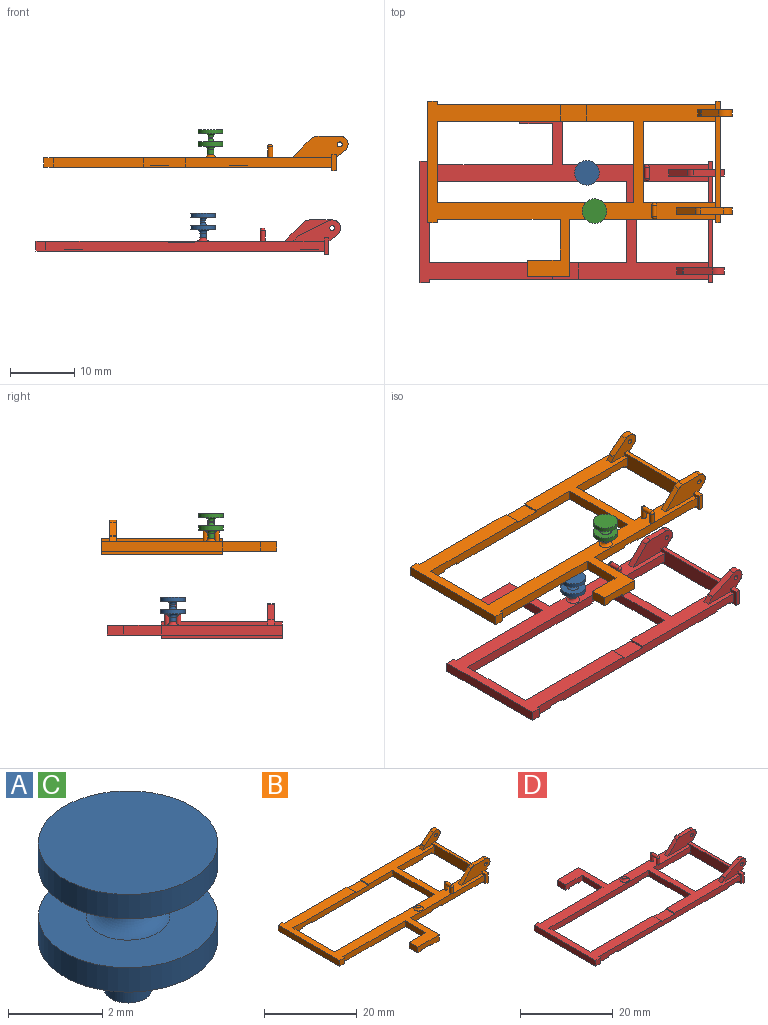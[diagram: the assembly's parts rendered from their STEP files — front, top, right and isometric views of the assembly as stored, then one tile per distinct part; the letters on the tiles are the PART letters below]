
ASSEMBLY  parts=4 mates=4
PART A: 12 faces, bbox 3.8x3.8x3.8 mm
  f0: cylinder r=0.51mm len=1.02mm, axis (0,0,-1), area 2.4mm2, adj f1,f11
  f1: plane 1.02x1.02mm, normal (0,0,-1), area 0.8mm2, adj f0
  f2: cylinder r=1.91mm len=3.81mm, axis (0,0,-1), area 7.6mm2, adj f3,f4
  f3: plane 3.81x3.81mm, normal (0,0,1), area 8.9mm2, adj f2,f9
  f4: plane 3.81x3.81mm, normal (0,0,-1), area 8.2mm2, adj f2,f11
  f5: cylinder r=0.38mm len=0.76mm, axis (0,0,-1), area 0.6mm2, adj f9,f10
  f6: cylinder r=1.91mm len=3.81mm, axis (0,0,-1), area 7.6mm2, adj f7,f8
  f7: plane 3.81x3.81mm, normal (0,0,1), area 11.4mm2, adj f6
  f8: plane 3.81x3.81mm, normal (0,0,-1), area 8.9mm2, adj f6,f10
  f9: torus R=0.89mm, axis (0,0,1), area 2.8mm2, adj f3,f5
  f10: torus R=0.89mm, axis (0,0,1), area 2.8mm2, adj f5,f8
  f11: torus R=1.02mm, axis (0,0,1), area 3.5mm2, adj f0,f4
PART B: 71 faces, bbox 47.2x27.2x5.3 mm
  f0: plane 44.7x27.18mm, normal (0,0,1), area 270.3mm2, adj f1,f2,f8,f9,f10,f16,f21,f22
  f1: plane 43.18x1.52mm, normal (0,1,0), area 63.4mm2, adj f0,f4,f5,f6,f16,f21,f47,f48
  f2: plane 5.3x3.3mm, normal (0,1,0), area 9.7mm2, adj f0,f11,f12,f13,f14,f15,f16,f17
  f3: cylinder r=1.27mm len=2.26mm, axis (0,-1,0), area 3.2mm2, adj f18,f41,f42,f56
  f4: plane 2.54x0.89mm, normal (0,0,-1), area 2.3mm2, adj f1,f16,f34,f50
  f5: plane 37.47x17.78mm, normal (0,0,-1), area 138.4mm2, adj f1,f10,f16,f30,f33,f34,f36,f37
  f6: plane 28.83x27.18mm, normal (0,0,-1), area 121.9mm2, adj f1,f8,f9,f10,f21,f22,f23,f24
  f7: plane 2.54x1.14mm, normal (0,0,-1), area 2.9mm2, adj f8,f9,f28,f53
  f8: plane 5.08x1.52mm, normal (0,1,0), area 7mm2, adj f0,f6,f7,f27,f28,f53,f54,f55
  f9: plane 6.6x1.52mm, normal (0,-1,0), area 9.4mm2, adj f0,f6,f7,f28,f29,f53,f54,f55
  f10: plane 30.48x1.52mm, normal (0,1,0), area 45.7mm2, adj f0,f5,f6,f35,f37,f44,f45,f46
  f11: plane 1.3x1.04mm, normal (0.62,0,-0.78), area 1.7mm2, adj f2,f12,f15,f43
  f12: cylinder r=1.27mm len=2.26mm, axis (0,-1,0), area 4.1mm2, adj f2,f11,f14,f43
  f13: cylinder r=0.38mm len=1.02mm, axis (0,-1,0), area 2.4mm2, adj f2,f43
  f14: plane 2.65x2.12mm, normal (-0.62,0,0.78), area 3.4mm2, adj f2,f12,f43,f59
  f15: plane 18.8x2.54mm, normal (1,0,0), area 46.7mm2, adj f2,f11,f17,f18,f20,f31,f32,f39
  f16: plane 18.8x2.54mm, normal (-1,0,0), area 39mm2, adj f0,f1,f2,f4,f5,f17,f20,f30
  f17: plane 1.27x0.76mm, normal (0,0,1), area 1mm2, adj f2,f15,f16,f32
  f18: plane 1.3x1.04mm, normal (0.62,0,-0.78), area 1.7mm2, adj f3,f15,f41,f42
  f19: cylinder r=0.38mm len=1.02mm, axis (0,-1,0), area 2.4mm2, adj f41,f42
  f20: plane 14.22x0.76mm, normal (0,0,1), area 10.8mm2, adj f15,f16,f42,f43
  f21: plane 1.52x0.51mm, normal (1,0,0), area 0.8mm2, adj f0,f1,f6,f22
  f22: plane 1.52x1.52mm, normal (0,1,0), area 2.3mm2, adj f0,f6,f21,f23
  f23: plane 18.8x1.52mm, normal (-1,0,0), area 28.6mm2, adj f0,f6,f22,f24
  f24: plane 1.52x1.52mm, normal (0,-1,0), area 2.3mm2, adj f0,f6,f23,f25
  f25: plane 1.52x0.51mm, normal (1,0,0), area 0.8mm2, adj f0,f6,f24,f26
  f26: plane 19.05x1.52mm, normal (0,-1,0), area 29mm2, adj f0,f6,f25,f27
  f27: plane 6.35x1.52mm, normal (-1,0,0), area 9.7mm2, adj f0,f6,f8,f26
  f28: plane 2.54x1.52mm, normal (-1,0,0), area 3.9mm2, adj f0,f7,f8,f9
  f29: plane 8.89x1.52mm, normal (1,0,0), area 13.5mm2, adj f0,f6,f9,f30
  f30: plane 22.61x1.52mm, normal (0,-1,0), area 33.7mm2, adj f0,f5,f6,f16,f29,f44,f45,f46
  f31: plane 2.54x0.76mm, normal (0,-1,0), area 1.9mm2, adj f15,f16,f39,f40
  f32: plane 2.54x0.76mm, normal (0,1,0), area 1.9mm2, adj f15,f16,f17,f39
  f33: plane 12.7x1.52mm, normal (1,0,0), area 19.4mm2, adj f0,f5,f34,f38
  f34: plane 11.18x1.52mm, normal (0,-1,0), area 16.3mm2, adj f0,f4,f5,f16,f33,f50,f51,f52
  f35: plane 12.7x1.52mm, normal (1,0,0), area 19.4mm2, adj f0,f6,f10,f36
  f36: plane 30.48x1.52mm, normal (0,-1,0), area 44.7mm2, adj f0,f5,f6,f35,f37,f47,f48,f49
  f37: plane 12.7x1.52mm, normal (-1,0,0), area 19.4mm2, adj f0,f5,f10,f36
  f38: plane 11.18x1.52mm, normal (0,1,0), area 17mm2, adj f0,f5,f16,f33
  f39: plane 18.8x0.76mm, normal (0,0,-1), area 14.3mm2, adj f15,f16,f31,f32
  f40: plane 1.27x0.76mm, normal (0,0,1), area 1mm2, adj f15,f16,f31,f41
  f41: plane 8.65x3.3mm, normal (0,-1,0), area 20.6mm2, adj f0,f3,f15,f16,f18,f19,f40,f56
  f42: plane 8.65x3.3mm, normal (0,1,0), area 20.6mm2, adj f0,f3,f15,f16,f18,f19,f20,f56
  f43: plane 5.3x3.3mm, normal (0,-1,0), area 9.7mm2, adj f0,f11,f12,f13,f14,f15,f16,f20
  f44: plane 2.54x0.25mm, normal (1,0,0), area 0.6mm2, adj f6,f10,f30,f46
  f45: plane 2.54x0.25mm, normal (-1,0,0), area 0.6mm2, adj f5,f10,f30,f46
  f46: plane 2.79x2.54mm, normal (0,0,-1), area 7.1mm2, adj f10,f30,f44,f45
  f47: plane 2.54x0.25mm, normal (-1,0,0), area 0.6mm2, adj f1,f5,f36,f49
  f48: plane 2.54x0.25mm, normal (1,0,0), area 0.6mm2, adj f1,f6,f36,f49
  f49: plane 2.79x2.54mm, normal (0,0,-1), area 7.1mm2, adj f1,f36,f47,f48
  f50: plane 2.54x0.25mm, normal (-1,0,0), area 0.6mm2, adj f1,f4,f34,f52
  f51: plane 2.54x0.25mm, normal (1,0,0), area 0.6mm2, adj f1,f5,f34,f52
  f52: plane 2.79x2.54mm, normal (0,0,-1), area 7.1mm2, adj f1,f34,f50,f51
  f53: plane 2.54x0.25mm, normal (1,0,0), area 0.6mm2, adj f7,f8,f9,f55
  f54: plane 2.54x0.25mm, normal (-1,0,0), area 0.6mm2, adj f6,f8,f9,f55
  f55: plane 2.79x2.54mm, normal (0,0,-1), area 7.1mm2, adj f8,f9,f53,f54
  f56: plane 3.56x1.02mm, normal (0,0,1), area 3.6mm2, adj f3,f41,f42,f57
  f57: cylinder r=1.27mm len=1.02mm, axis (0,-1,0), area 1mm2, adj f41,f42,f56,f58
  f58: plane 2.93x2.93mm, normal (-0.71,0,0.71), area 4.2mm2, adj f0,f41,f42,f57
  f59: cylinder r=0.51mm len=1.02mm, axis (0,1,0), area 0.2mm2, adj f2,f14,f43,f60
  f60: plane 1.02x0.77mm, normal (-0.85,0,0.52), area 0.9mm2, adj f0,f2,f43,f59
  f61: plane 2.54x0.25mm, normal (-1,0,0), area 0.6mm2, adj f0,f1,f36,f63
  f62: plane 2.54x0.25mm, normal (1,0,0), area 0.6mm2, adj f0,f1,f36,f63
  f63: plane 4.06x2.54mm, normal (0,0,1), area 10.3mm2, adj f1,f36,f61,f62
  f64: plane 1.02x1.02mm, normal (0,0,1), area 0.8mm2, adj f65
  f65: torus R=1.02mm, axis (0,0,1), area 3.5mm2, adj f0,f64
  f66: cylinder r=0.38mm len=1.65mm, axis (0,0,-1), area 3.7mm2, adj f0,f69,f70
  f67: sphere r=0.38mm, area 0.5mm2, adj f68,f70
  f68: cylinder r=0.38mm len=1.65mm, axis (0,0,1), area 3.7mm2, adj f0,f67,f70
  f69: sphere r=0.38mm, area 0.5mm2, adj f66,f70
  f70: cylinder r=0.38mm len=1.78mm, axis (0,-1,0), area 3.7mm2, adj f66,f67,f68,f69
PART C: same geometry as A
PART D: 71 faces, bbox 47.2x27.2x5.3 mm
  f0: plane 44.7x27.18mm, normal (0,0,1), area 268.2mm2, adj f2,f3,f8,f9,f10,f11,f16,f22
  f1: plane 4.57x2.21mm, normal (-0.44,0,0.9), area 5.2mm2, adj f2,f19,f41,f62
  f2: plane 7.37x3.3mm, normal (0,-1,0), area 13.4mm2, adj f0,f1,f15,f16,f18,f19,f20,f40
  f3: plane 30.48x1.52mm, normal (0,1,0), area 44.7mm2, adj f0,f4,f6,f35,f37,f44,f45,f46
  f4: plane 28.83x27.18mm, normal (0,0,-1), area 121.9mm2, adj f3,f8,f9,f10,f22,f23,f24,f25
  f5: plane 2.54x1.14mm, normal (0,0,-1), area 2.9mm2, adj f9,f10,f32,f54
  f6: plane 37.47x17.78mm, normal (0,0,-1), area 138.4mm2, adj f3,f8,f11,f16,f28,f33,f34,f36
  f7: plane 2.54x0.89mm, normal (0,0,-1), area 2.3mm2, adj f11,f16,f28,f47
  f8: plane 22.61x1.52mm, normal (0,1,0), area 33.7mm2, adj f0,f4,f6,f16,f31,f50,f51,f52
  f9: plane 6.6x1.52mm, normal (0,1,0), area 9.4mm2, adj f0,f4,f5,f31,f32,f53,f54,f55
  f10: plane 5.08x1.52mm, normal (0,-1,0), area 7mm2, adj f0,f4,f5,f32,f38,f53,f54,f55
  f11: plane 11.18x1.52mm, normal (0,1,0), area 16.3mm2, adj f0,f6,f7,f16,f33,f47,f48,f49
  f12: plane 1.3x1.04mm, normal (0.62,0,-0.78), area 1.7mm2, adj f13,f15,f42,f43
  f13: cylinder r=1.27mm len=2.26mm, axis (0,-1,0), area 3.2mm2, adj f12,f42,f43,f58
  f14: cylinder r=0.38mm len=1.02mm, axis (0,-1,0), area 2.4mm2, adj f42,f43
  f15: plane 18.8x2.54mm, normal (1,0,0), area 46.7mm2, adj f2,f12,f17,f18,f21,f29,f30,f39
  f16: plane 18.8x2.54mm, normal (-1,0,0), area 39mm2, adj f0,f2,f6,f7,f8,f11,f17,f21
  f17: plane 1.27x0.76mm, normal (0,0,1), area 1mm2, adj f15,f16,f30,f43
  f18: plane 1.3x1.04mm, normal (0.62,0,-0.78), area 1.7mm2, adj f2,f15,f19,f41
  f19: cylinder r=1.27mm len=2.26mm, axis (0,-1,0), area 3.8mm2, adj f1,f2,f18,f41
  f20: cylinder r=0.38mm len=1.02mm, axis (0,-1,0), area 2.4mm2, adj f2,f41
  f21: plane 14.22x0.76mm, normal (0,0,1), area 10.8mm2, adj f15,f16,f41,f42
  f22: plane 19.05x1.52mm, normal (0,1,0), area 29mm2, adj f0,f4,f23,f38
  f23: plane 1.52x0.51mm, normal (1,0,0), area 0.8mm2, adj f0,f4,f22,f24
  f24: plane 1.52x1.52mm, normal (0,1,0), area 2.3mm2, adj f0,f4,f23,f25
  f25: plane 18.8x1.52mm, normal (-1,0,0), area 28.6mm2, adj f0,f4,f24,f26
  f26: plane 1.52x1.52mm, normal (0,-1,0), area 2.3mm2, adj f0,f4,f25,f27
  f27: plane 1.52x0.51mm, normal (1,0,0), area 0.8mm2, adj f0,f4,f26,f28
  f28: plane 43.18x1.52mm, normal (0,-1,0), area 63.4mm2, adj f0,f4,f6,f7,f16,f27,f44,f45
  f29: plane 2.54x0.76mm, normal (0,-1,0), area 1.9mm2, adj f15,f16,f39,f40
  f30: plane 2.54x0.76mm, normal (0,1,0), area 1.9mm2, adj f15,f16,f17,f39
  f31: plane 8.89x1.52mm, normal (1,0,0), area 13.5mm2, adj f0,f4,f8,f9
  f32: plane 2.54x1.52mm, normal (-1,0,0), area 3.9mm2, adj f0,f5,f9,f10
  f33: plane 12.7x1.52mm, normal (1,0,0), area 19.4mm2, adj f0,f6,f11,f34
  f34: plane 11.18x1.52mm, normal (0,-1,0), area 17mm2, adj f0,f6,f16,f33
  f35: plane 12.7x1.52mm, normal (1,0,0), area 19.4mm2, adj f0,f3,f4,f36
  f36: plane 30.48x1.52mm, normal (0,-1,0), area 45.7mm2, adj f0,f4,f6,f35,f37,f50,f51,f52
  f37: plane 12.7x1.52mm, normal (-1,0,0), area 19.4mm2, adj f0,f3,f6,f36
  f38: plane 6.35x1.52mm, normal (-1,0,0), area 9.7mm2, adj f0,f4,f10,f22
  f39: plane 18.8x0.76mm, normal (0,0,-1), area 14.3mm2, adj f15,f16,f29,f30
  f40: plane 1.27x0.76mm, normal (0,0,1), area 1mm2, adj f2,f15,f16,f29
  f41: plane 7.37x3.3mm, normal (0,1,0), area 13.4mm2, adj f0,f1,f15,f16,f18,f19,f20,f21
  f42: plane 8.65x3.3mm, normal (0,-1,0), area 20.6mm2, adj f0,f12,f13,f14,f15,f16,f21,f56
  f43: plane 8.65x3.3mm, normal (0,1,0), area 20.6mm2, adj f0,f12,f13,f14,f15,f16,f17,f56
  f44: plane 2.54x0.25mm, normal (-1,0,0), area 0.6mm2, adj f3,f6,f28,f46
  f45: plane 2.54x0.25mm, normal (1,0,0), area 0.6mm2, adj f3,f4,f28,f46
  f46: plane 2.79x2.54mm, normal (0,0,-1), area 7.1mm2, adj f3,f28,f44,f45
  f47: plane 2.54x0.25mm, normal (-1,0,0), area 0.6mm2, adj f7,f11,f28,f49
  f48: plane 2.54x0.25mm, normal (1,0,0), area 0.6mm2, adj f6,f11,f28,f49
  f49: plane 2.79x2.54mm, normal (0,0,-1), area 7.1mm2, adj f11,f28,f47,f48
  f50: plane 2.54x0.25mm, normal (-1,0,0), area 0.6mm2, adj f6,f8,f36,f52
  f51: plane 2.54x0.25mm, normal (1,0,0), area 0.6mm2, adj f4,f8,f36,f52
  f52: plane 2.79x2.54mm, normal (0,0,-1), area 7.1mm2, adj f8,f36,f50,f51
  f53: plane 2.54x0.25mm, normal (-1,0,0), area 0.6mm2, adj f4,f9,f10,f55
  f54: plane 2.54x0.25mm, normal (1,0,0), area 0.6mm2, adj f5,f9,f10,f55
  f55: plane 2.79x2.54mm, normal (0,0,-1), area 7.1mm2, adj f9,f10,f53,f54
  f56: plane 2.93x2.93mm, normal (-0.71,0,0.71), area 4.2mm2, adj f0,f42,f43,f57
  f57: cylinder r=1.27mm len=1.02mm, axis (0,1,0), area 1mm2, adj f42,f43,f56,f58
  f58: plane 3.56x1.02mm, normal (0,0,1), area 3.6mm2, adj f13,f42,f43,f57
  f59: plane 2.54x0.25mm, normal (-1,0,0), area 0.6mm2, adj f0,f3,f28,f61
  f60: plane 2.54x0.25mm, normal (1,0,0), area 0.6mm2, adj f0,f3,f28,f61
  f61: plane 4.06x2.54mm, normal (0,0,1), area 10.3mm2, adj f3,f28,f59,f60
  f62: cylinder r=0.51mm len=1.02mm, axis (0,-1,0), area 0.2mm2, adj f1,f2,f41,f63
  f63: plane 1.02x0.86mm, normal (-0.72,0,0.7), area 1.2mm2, adj f0,f2,f41,f62
  f64: plane 1.02x1.02mm, normal (0,0,1), area 0.8mm2, adj f65
  f65: torus R=1.02mm, axis (0,0,1), area 3.5mm2, adj f0,f64
  f66: cylinder r=0.38mm len=1.65mm, axis (0,0,-1), area 3.7mm2, adj f0,f69,f70
  f67: sphere r=0.38mm, area 0.5mm2, adj f68,f70
  f68: cylinder r=0.38mm len=1.65mm, axis (0,0,1), area 3.7mm2, adj f0,f67,f70
  f69: sphere r=0.38mm, area 0.5mm2, adj f66,f70
  f70: cylinder r=0.38mm len=1.78mm, axis (0,-1,0), area 3.7mm2, adj f66,f67,f68,f69
PLACE A t=(-6.43,4.09,5.57)mm
PLACE B t=(-9.32,-3.15,16.53)mm
PLACE C t=(-5.25,-1.88,18.57)mm
PLACE D t=(-10.5,-12.42,3.54)mm
MATE planar A.f0 <-> D.f65  axis (0,0,-1) through (-6.43,4.09,5.57)mm
MATE cylindrical A.f0 <-> D.f65  axis (0,0,-1) through (-6.43,4.09,5.57)mm
MATE planar B.f65 <-> C.f0  axis (0,0,1) through (-5.25,-1.88,18.57)mm
MATE cylindrical C.f0 <-> B.f65  axis (0,0,-1) through (-5.25,-1.88,18.57)mm
